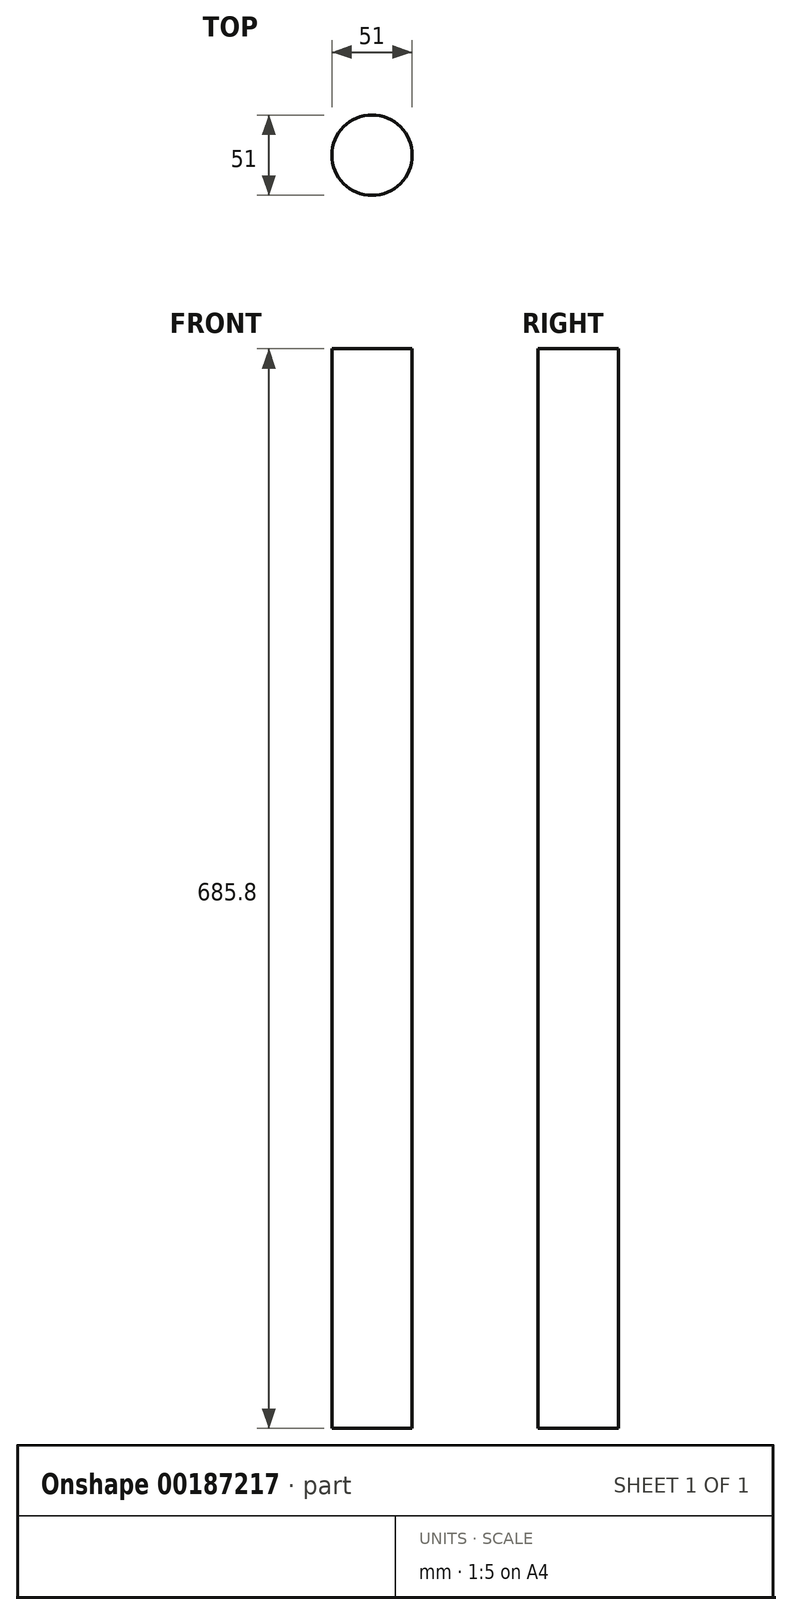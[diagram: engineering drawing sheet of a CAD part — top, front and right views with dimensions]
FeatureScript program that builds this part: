
annotation { "Feature Type Name" : "Feature", "Feature Type Description" : "" }
export const myFeature = defineFeature(function(context is Context, id is Id, definition is map)
    precondition{}
    {
        {
            var Q0;
            Q0=qCreatedBy(makeId("Top.planeOp"),FACE);
            var sketch = newSketch(context, id + "F0", { "sketchPlane" : qUnion([Q0])});
            skCircle(sketch, "E0", {"center": v(0, 0) * mm, "radius": 25.5 * mm});
            skCircle(sketch, "E1", {"center": v(0, 0) * mm, "radius": 7.97 * mm});
            skSolve(sketch);
        }
        {
            var Q0;
            Q0=makeQuery(id+"F0.imprint","IMPRINT",FACE,{"disambiguationData":[TD([[makeQuery(id+"F0.imprint","IMPRINT",EDGE,{"derivedFrom":sQuery(id+"F0.wireOp",EDGE,"E0")}),1.0]])]});
            var Q1;
            Q1=makeQuery(id+"F0.imprint","IMPRINT",FACE,{"disambiguationData":[TD([[makeQuery(id+"F0.imprint","IMPRINT",EDGE,{"derivedFrom":sQuery(id+"F0.wireOp",EDGE,"E1")}),1.0]])]});
            extrude(context, id + "F1", {"entities" : qUnion([Q0, Q1]), "depth" : 50.8 * mm});
        }
        {
            var Q0;
            Q0=makeQuery(id+"F1.opExtrude","CAP_FACE",FACE,{"disambiguationData":[OSD([sQuery(id+"F0.wireOp",EDGE,"E0")])],"isStart":false});
            var Q1;
            Q1=makeQuery(id+"F1.opExtrude","CAP_FACE",FACE,{"disambiguationData":[OSD([sQuery(id+"F0.wireOp",EDGE,"E0")])],"isStart":true});
            extrude(context, id + "F2", {"entities" : qUnion([Q0, Q1]), "operationType" : NewBodyOperationType.ADD, "depth" : 635 * mm});
        }
    });
